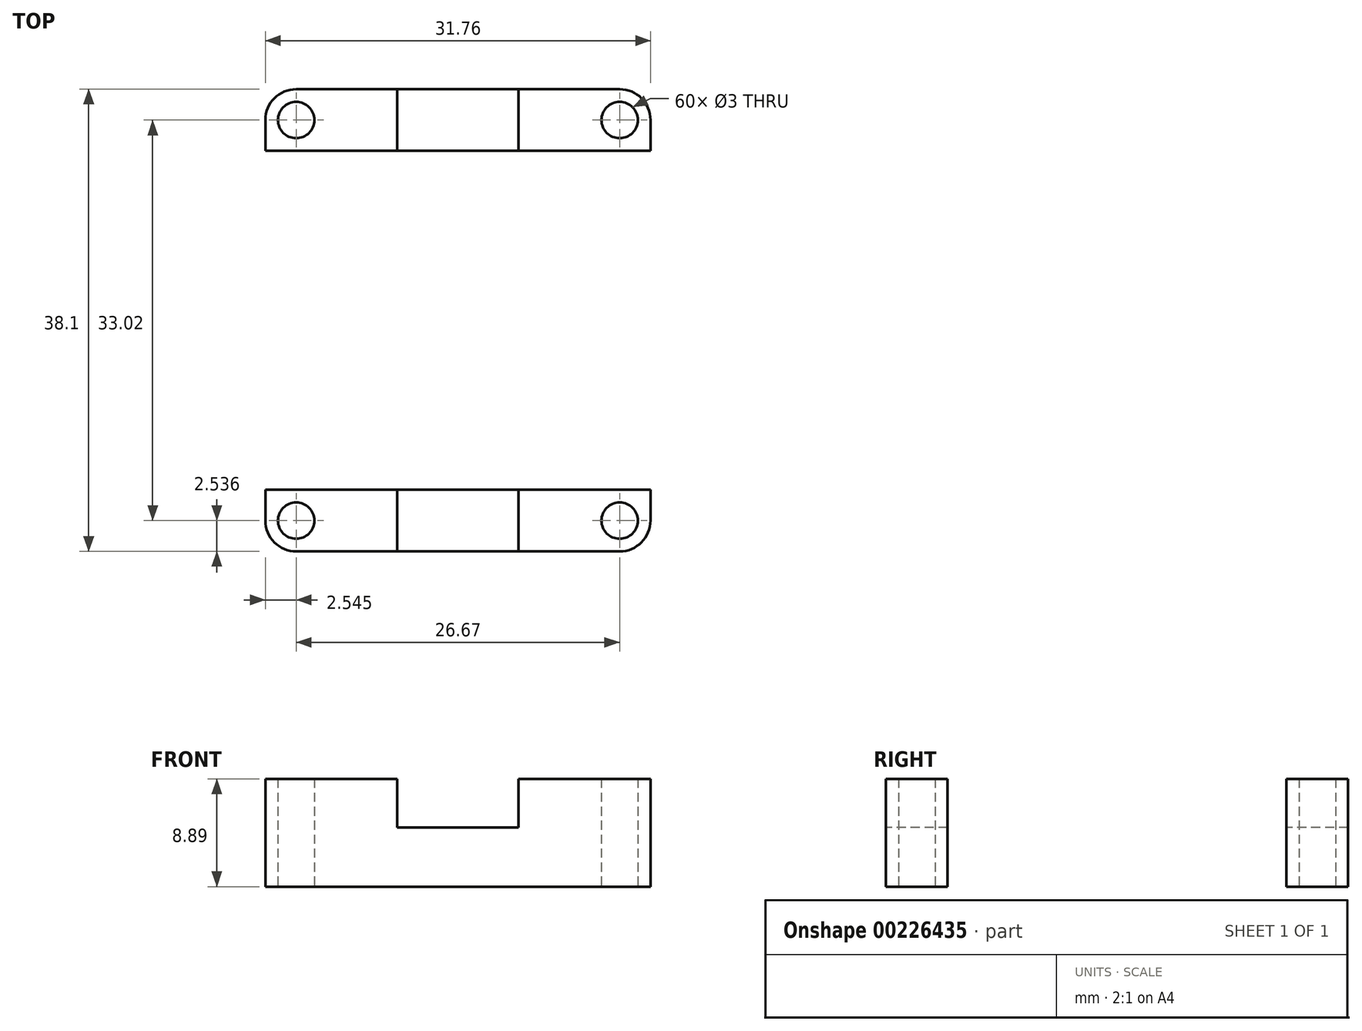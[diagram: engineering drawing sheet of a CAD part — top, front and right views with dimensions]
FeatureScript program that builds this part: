
annotation { "Feature Type Name" : "Feature", "Feature Type Description" : "" }
export const myFeature = defineFeature(function(context is Context, id is Id, definition is map)
    precondition{}
    {
        {
            var Q0;
            Q0=qCreatedBy(makeId("Top.planeOp"),FACE);
            var sketch = newSketch(context, id + "F0", { "sketchPlane" : qUnion([Q0])});
            skLineSegment(sketch, "E0.bottom", {"start": v(15.88, 15.7) * mm, "end": v(-15.88, 15.7) * mm});
            skLineSegment(sketch, "E0.top", {"start": v(13.33, 20.79) * mm, "end": v(-13.34, 20.79) * mm});
            skLineSegment(sketch, "E0.left", {"start": v(15.87, 15.7) * mm, "end": v(15.87, 18.25) * mm});
            skLineSegment(sketch, "E0.right", {"start": v(-15.88, 15.7) * mm, "end": v(-15.88, 18.25) * mm});
            skPoint(sketch, "E0.middle", {"position": v(0, 18.25) * mm});
            skLineSegment(sketch, "E1.bottom", {"start": v(13.34, -17.31) * mm, "end": v(-13.33, -17.31) * mm});
            skLineSegment(sketch, "E1.top", {"start": v(15.88, -12.23) * mm, "end": v(-15.87, -12.23) * mm});
            skLineSegment(sketch, "E1.left", {"start": v(15.88, -14.77) * mm, "end": v(15.88, -12.23) * mm});
            skLineSegment(sketch, "E1.right", {"start": v(-15.87, -14.77) * mm, "end": v(-15.87, -12.23) * mm});
            skPoint(sketch, "E1.middle", {"position": v(0, -14.77) * mm});
            skPoint(sketch, "E2.visualSharp", {"position": v(15.88, 20.79) * mm});
            skArc(sketch, "E2.filletArc", {"start": v(15.87, 18.25) * mm, "mid": v(15.13, 20.04) * mm, "end": v(13.33, 20.79) * mm});
            skPoint(sketch, "E3.visualSharp", {"position": v(-15.88, 20.79) * mm});
            skArc(sketch, "E3.filletArc", {"start": v(-13.34, 20.79) * mm, "mid": v(-15.13, 20.04) * mm, "end": v(-15.88, 18.25) * mm});
            skPoint(sketch, "E4.visualSharp", {"position": v(-15.87, -17.31) * mm});
            skArc(sketch, "E4.filletArc", {"start": v(-15.87, -14.77) * mm, "mid": v(-15.13, -16.57) * mm, "end": v(-13.33, -17.31) * mm});
            skPoint(sketch, "E5.visualSharp", {"position": v(15.88, -17.31) * mm});
            skArc(sketch, "E5.filletArc", {"start": v(13.34, -17.31) * mm, "mid": v(15.13, -16.57) * mm, "end": v(15.88, -14.77) * mm});
            skCircle(sketch, "E6", {"center": v(-13.33, 18.25) * mm, "radius": 1.5 * mm});
            skCircle(sketch, "E7", {"center": v(13.33, 18.25) * mm, "radius": 1.5 * mm});
            skCircle(sketch, "E8", {"center": v(13.34, -14.77) * mm, "radius": 1.5 * mm});
            skCircle(sketch, "E9", {"center": v(-13.33, -14.77) * mm, "radius": 1.5 * mm});
            skSolve(sketch);
        }
        {
            var Q0;
            Q0=makeQuery(id+"F0.imprint","IMPRINT",FACE,{"disambiguationData":[TD([[makeQuery(id+"F0.imprint","IMPRINT",EDGE,{"derivedFrom":sQuery(id+"F0.wireOp",EDGE,"E0.bottom")}),-1.0]])]});
            var Q1;
            Q1=makeQuery(id+"F0.imprint","IMPRINT",FACE,{"disambiguationData":[TD([[makeQuery(id+"F0.imprint","IMPRINT",EDGE,{"derivedFrom":sQuery(id+"F0.wireOp",EDGE,"E1.bottom")}),-1.0]])]});
            extrude(context, id + "F1", {"entities" : qUnion([Q0, Q1]), "depth" : 8.9 * mm, "offsetDistance" : 25.4 * mm});
        }
        {
            var Q0;
            Q0=makeQuery(id+"F1.opExtrude","SWEPT_FACE",FACE,{"disambiguationData":[OSD([sQuery(id+"F0.wireOp",EDGE,"E1.bottom")])]});
            var sketch = newSketch(context, id + "F2", { "sketchPlane" : qUnion([Q0])});
            skLineSegment(sketch, "E10.bottom", {"start": v(5, 4.89) * mm, "end": v(-5, 4.89) * mm});
            skLineSegment(sketch, "E10.top", {"start": v(5, 12.9) * mm, "end": v(-5, 12.9) * mm});
            skLineSegment(sketch, "E10.left", {"start": v(5, 4.89) * mm, "end": v(5, 12.9) * mm});
            skLineSegment(sketch, "E10.right", {"start": v(-5, 4.89) * mm, "end": v(-5, 12.9) * mm});
            skPoint(sketch, "E10.middle", {"position": v(0, 8.9) * mm});
            skSolve(sketch);
        }
        {
            var Q0;
            {var subQ0=sQuery(id+"F2.wireOp",EDGE,"E10.bottom");Q0=makeQuery(id+"F2.imprint","IMPRINT",FACE,{"disambiguationData":[TD([[makeQuery(id+"F2.imprint","IMPRINT",EDGE,{"derivedFrom":subQ0}),-1.0]])]});}
            extrude(context, id + "F3", {"entities" : qUnion([Q0]), "operationType" : NewBodyOperationType.REMOVE, "endBound" : BoundingType.THROUGH_ALL, "oppositeDirection" : true, "depth" : 25.4 * mm, "offsetDistance" : 25.4 * mm});
        }
    });
